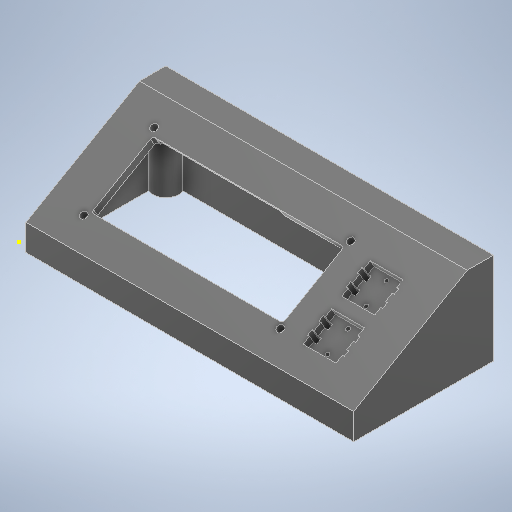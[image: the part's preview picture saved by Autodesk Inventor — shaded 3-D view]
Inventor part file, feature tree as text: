
AUTODESK INVENTOR PART (.ipt)
format: ipt  version: 2025.1 (Build 291241020, 241B)  size: 1,038,336 bytes
history: native  units: mm
features: sketch x16, extrude x11, projected_geometry x9, plane x6, hole x2, mirror x2, shell x1, fillet x1
ambient origin geometry x8: Origin, YZ Plane, XZ Plane, XY Plane, X Axis, Y Axis, Z Axis, Center Point
bodies: Solid1 (feature_tree)
feature tree (48):
  extrude  "Extrusion1"  TaperAngle=30.0deg  [1 undecoded]
  shell  "Shell1"  Thickness=10.0mm
  extrude  "Extrusion2"  Depth=3.0mm
  plane  "Work Plane1"
  plane  "Work Plane2"
  hole  "Hole1"  [1 undecoded]
  extrude  "Extrusion3"  Depth=11.5mm
  sketch  "Sketch5"  dims[d12=120.0mm d13=0.0mm d14=75.0mm]
  plane  "Work Plane3"
  plane  "Work Plane4"
  extrude  "Extrusion4"  Depth=75.0mm
  extrude  "Extrusion5"  Depth=37.0mm
  sketch  "Sketch9"  dims[d17=15.8mm]
  sketch  "Sketch10"  dims[d18=2.6mm d19=6.0mm d20=4.0mm d21=2.0mm d22=90.0deg d23=8.0mm d24=0.0mm d25=15.0mm]
  extrude  "Extrusion6"  Depth=15.0mm
  plane  "Work Plane5"
  mirror  "Mirror1"
  extrude  "Extrusion7"  Depth=10.0mm TaperAngle=0.0deg
  extrude  "Extrusion8"  Depth=12.0mm
  hole  "Hole2"  [1 undecoded]
  plane  "Work Plane6"
  mirror  "Mirror2"
  extrude  "Extrusion9"  Depth=6.0mm
  extrude  "Extrusion10"  Depth=1.0mm
  sketch  "Sketch17"  dims[d42=4.5mm]
  fillet  "Fillet1"  Radius=7.0mm
  extrude  "Extrusion11"  Depth=1.45mm
  sketch  "Sketch1"  dims[d0=10.0mm d2=30.0deg d3=10.0mm]
  sketch  "Sketch2"  dims[d4=125.0mm d5=0.0mm d6=3.0mm]
  sketch  "Sketch3"  dims[d7=50.0mm d8=27.0mm]
  sketch  "Sketch4"  dims[d9=73.0mm d11=11.5mm]
  sketch  "Sketch8"  dims[d15=31.0mm d16=37.0mm]
  sketch  "Sketch11"  dims[d26=3.0mm d27=0.0mm d28=10.0mm d29=0.0mm]
  sketch  "Sketch12"  dims[d30=2.0mm d31=0.0mm d32=12.0mm]
  sketch  "Sketch13"  dims[d33=12.0mm d34=7.0mm]
  sketch  "Sketch14"  dims[d35=6.0mm d36=6.0mm]
  sketch  "Sketch15"  dims[d37=1.0mm d38=1.0mm d39=7.0mm]
  sketch  "Sketch16"  dims[d40=1.45mm d41=1.45mm]
  projected_geometry  "Projected Loop1"
  projected_geometry  "Projected Loop2"
  projected_geometry  "Projected Loop3"
  projected_geometry  "Projected Loop4"
  projected_geometry  "Projected Loop5"
  projected_geometry  "Projected Loop6"
  projected_geometry  "Projected Loop7"
  projected_geometry  "Projected Loop8"
  sketch  "Sketch18"  dims[d43=4.5mm d44=2.7mm d45=2.0mm d46=0.5mm d47=135.0deg d48=1.992893mm d49=0.5mm d50=10.0mm d51=10.0mm d52=6.0mm d53=135.0deg d54=1.0mm d55=0.5mm d56=1.0mm d57=12.0mm d58=0.5mm d59=6.0mm d60=10.0mm d62=10.0mm d64=1.0mm d65=2.0mm d66=2.5mm d67=1.0mm d68=2.0mm d69=2.5mm d70=1.0mm d71=1.0mm d72=10.0mm d73=10.0mm d74=0.0mm d75=0.0mm d76=20.0mm d78=6.0mm d79=6.0mm d80=4.0mm d81=2.0mm d82=2.0mm d83=10.0mm d84=5.0mm d85=5.0mm d86=3.0mm d87=0.0mm d88=10.0mm d89=5.0mm d90=5.0mm d91=10.0mm d92=0.0mm d95=4.8mm d96=6.0mm d97=4.0mm d98=2.0mm d99=90.0deg d100=8.0mm d101=0.0mm d102=12.5mm d103=9.75mm d104=0.25mm d105=2.25mm d106=3.0mm d107=0.0mm d108=3.0mm d109=0.0mm d110=1.0mm d113=3.5mm d115=3.0mm d116=50.0mm d117=2.0mm d118=0.0mm]
  projected_geometry  "Projected Loop9"
note: 3 required parameter values undecoded (feature->parameter linkage not recoverable at this tier; creation-order binding heuristic only, values carry confidence <= 0.55)
